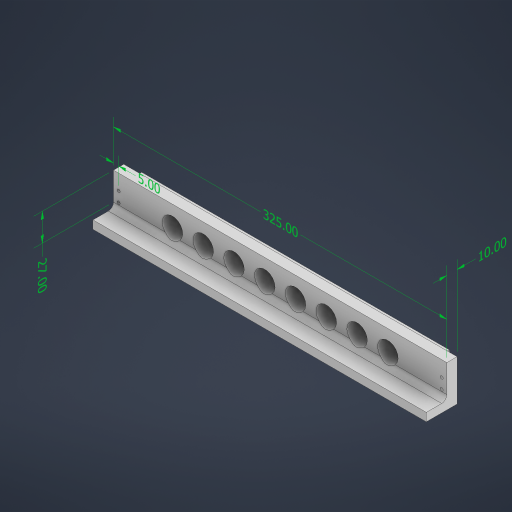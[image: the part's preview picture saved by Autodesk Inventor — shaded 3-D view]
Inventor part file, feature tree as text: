
AUTODESK INVENTOR PART (.ipt)
format: ipt  version: 2023 (Build 270158000, 158)  size: 309,248 bytes
history: native  units: mm
features: other x5, extrude x5, sketch x5, thread x4, fillet x1
ambient origin geometry x8: Origin, YZ Plane, XZ Plane, XY Plane, X Axis, Y Axis, Z Axis, Center Point
bodies: Solid1 (feature_tree)
feature tree (20):
  other  "Annotations"
  extrude  "Extrusion1"  Depth=10.0mm
  extrude  "Extrusion3"  Depth=8.0mm
  extrude  "Extrusion4"  Depth=10.0mm
  thread  "Thread1"  [1 undecoded]
  thread  "Thread2"  [1 undecoded]
  thread  "Thread3"  [1 undecoded]
  thread  "Thread4"  [1 undecoded]
  extrude  "Extrusion5"  Depth=3.0mm
  extrude  "Extrusion6"  Depth=10.0mm
  fillet  "Fillet2"  Radius=15.0mm
  sketch  "Sketch1"  dims[d0=325.0mm d1=10.0mm]
  sketch  "Sketch4"  dims[d2=40.0mm d3=0.0mm d34=8.0mm]
  sketch  "Sketch5"  dims[d35=20.0mm d36=0.0mm d39=3.0mm d40=3.0mm d41=5.0mm d42=5.0mm d43=10.0mm]
  sketch  "Sketch8"  dims[d44=15.0mm d45=3.0mm]
  sketch  "Sketch9"  dims[d46=3.0mm d47=10.0mm d48=15.0mm d49=5.0mm d50=5.0mm d51=20.0mm d52=0.0mm d53=10.0mm d54=0.0mm d55=10.0mm d56=0.0mm d57=10.0mm d58=0.0mm d59=10.0mm d60=0.0mm d67=300.0mm d68=37.0mm d69=12.5mm d70=12.5mm d71=3.0mm d72=5.0mm d73=0.0mm d74=20.0mm d75=20.0mm d76=20.0mm d77=20.0mm d78=20.0mm d79=20.0mm d80=20.0mm d81=20.0mm d82=30.0mm d83=30.0mm d84=30.0mm d85=30.0mm d86=30.0mm d87=30.0mm d88=30.0mm d89=57.5mm d90=20.0mm d91=57.5mm d92=40.0mm d93=0.0mm d94=5.0mm d25=0.0mm d26=10.0mm d27=27.0mm d28=0.0mm d29=10.0mm d30=325.0mm d31=0.0mm d32=10.0mm d33=10.0mm d61=6.949513mm d62=5.0mm]
  other  "Linear Dimension 1"
  other  "Linear Dimension 2"
  other  "Linear Dimension 3"
  other  "Linear Dimension 4"
note: 4 required parameter values undecoded (feature->parameter linkage not recoverable at this tier; creation-order binding heuristic only, values carry confidence <= 0.55)
